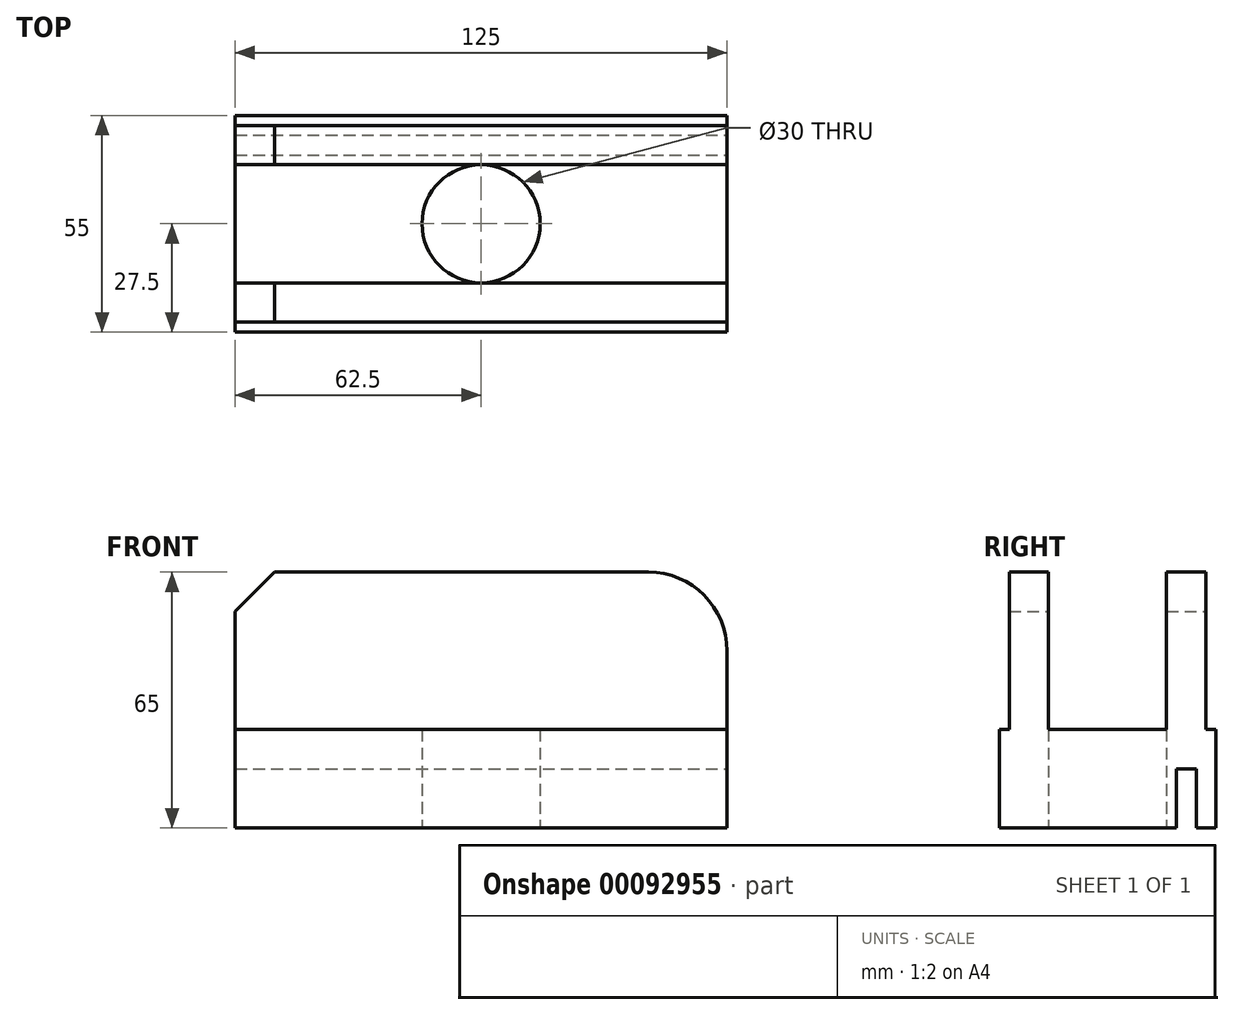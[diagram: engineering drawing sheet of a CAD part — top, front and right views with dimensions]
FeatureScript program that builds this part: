
annotation { "Feature Type Name" : "Feature", "Feature Type Description" : "" }
export const myFeature = defineFeature(function(context is Context, id is Id, definition is map)
    precondition{}
    {
        {
            var Q0;
            Q0=qCreatedBy(makeId("Top.planeOp"),FACE);
            var sketch = newSketch(context, id + "F0", { "sketchPlane" : qUnion([Q0])});
            skLineSegment(sketch, "E0.bottom", {"start": v(62.5, -27.5) * mm, "end": v(-62.5, -27.5) * mm});
            skLineSegment(sketch, "E0.top", {"start": v(62.5, 27.5) * mm, "end": v(-62.5, 27.5) * mm});
            skLineSegment(sketch, "E0.left", {"start": v(62.5, -27.5) * mm, "end": v(62.5, 27.5) * mm});
            skLineSegment(sketch, "E0.right", {"start": v(-62.5, -27.5) * mm, "end": v(-62.5, 27.5) * mm});
            skPoint(sketch, "E0.middle", {"position": v(0, 0) * mm});
            skCircle(sketch, "E1", {"center": v(0, 0) * mm, "radius": 15 * mm});
            skSolve(sketch);
        }
        {
            var Q0;
            Q0=qSketchRegion(id+"F0",true);
            extrude(context, id + "F1", {"entities" : qUnion([Q0]), "depth" : 25 * mm});
        }
        {
            var Q0;
            Q0=makeQuery(id+"F1.opExtrude","CAP_FACE",FACE,{"disambiguationData":[OSD([sQuery(id+"F0.wireOp",EDGE,"E0.bottom"),sQuery(id+"F0.wireOp",EDGE,"E0.top"),sQuery(id+"F0.wireOp",EDGE,"E0.left"),sQuery(id+"F0.wireOp",EDGE,"E0.right"),sQuery(id+"F0.wireOp",EDGE,"E1")])],"isStart":false});
            var sketch = newSketch(context, id + "F2", { "sketchPlane" : qUnion([Q0])});
            skLineSegment(sketch, "E2.bottom", {"start": v(-62.5, -25) * mm, "end": v(62.5, -25) * mm});
            skLineSegment(sketch, "E2.left", {"start": v(-62.5, -25) * mm, "end": v(-62.5, -15) * mm});
            skLineSegment(sketch, "E2.right", {"start": v(62.5, -25) * mm, "end": v(62.5, -15) * mm});
            skLineSegment(sketch, "E3.bottom", {"start": v(-62.5, -25) * mm, "end": v(-62.5, -25) * mm});
            skLineSegment(sketch, "E3.top", {"start": v(-62.5, -27.5) * mm, "end": v(-62.5, -27.5) * mm});
            skLineSegment(sketch, "E3.left", {"start": v(-62.5, -25) * mm, "end": v(-62.5, -27.5) * mm});
            skLineSegment(sketch, "E3.right", {"start": v(-62.5, -25) * mm, "end": v(-62.5, -27.5) * mm});
            skLineSegment(sketch, "E4", {"start": v(62.5, -15) * mm, "end": v(-62.5, -15) * mm});
            skLineSegment(sketch, "E5", {"start": v(0, 15) * mm, "end": v(62.5, 15) * mm});
            skLineSegment(sketch, "E6", {"start": v(62.5, 15) * mm, "end": v(62.5, 25) * mm});
            skLineSegment(sketch, "E7", {"start": v(62.5, 25) * mm, "end": v(-62.5, 25) * mm});
            skLineSegment(sketch, "E8", {"start": v(-62.5, 25) * mm, "end": v(-62.5, 15) * mm});
            skLineSegment(sketch, "E9", {"start": v(-62.5, 15) * mm, "end": v(0, 15) * mm});
            skSolve(sketch);
        }
        {
            var Q0;
            Q0=qSketchRegion(id+"F2",true);
            extrude(context, id + "F3", {"entities" : qUnion([Q0]), "operationType" : NewBodyOperationType.ADD, "depth" : 40 * mm});
        }
        {
            var Q0;
            Q0=makeQuery(id+"F3.opExtrude","CAP_EDGE",EDGE,{"disambiguationData":[OSD([sQuery(id+"F2.wireOp",EDGE,"E2.right")])],"isStart":false});
            var Q1;
            Q1=makeQuery(id+"F3.opExtrude","CAP_EDGE",EDGE,{"disambiguationData":[OSD([sQuery(id+"F2.wireOp",EDGE,"E6")])],"isStart":false});
            fillet(context, id + "F4", {"entities" : qUnion([Q0, Q1]), "radius" : 20 * mm, "tangentPropagation" : true, "allowEdgeOverflow" : false});
        }
        {
            var Q0;
            Q0=makeQuery(id+"F3.opExtrude","CAP_EDGE",EDGE,{"disambiguationData":[OSD([sQuery(id+"F2.wireOp",EDGE,"E8")])],"isStart":false});
            var Q1;
            Q1=makeQuery(id+"F3.opExtrude","CAP_EDGE",EDGE,{"disambiguationData":[OSD([sQuery(id+"F2.wireOp",EDGE,"E2.left")])],"isStart":false});
            chamfer(context, id + "F5", {"entities" : qUnion([Q0, Q1]), "width" : 10 * mm, "tangentPropagation" : true});
        }
        {
            var Q0;
            Q0=makeQuery(id+"F3.boolean.opBoolean","MERGE",FACE,{"derivedFrom":[makeQuery(id+"F1.opExtrude","SWEPT_FACE",FACE,{"disambiguationData":[OSD([sQuery(id+"F0.wireOp",EDGE,"E0.left")])]}),makeQuery(id+"F3.opExtrude","SWEPT_FACE",FACE,{"disambiguationData":[OSD([sQuery(id+"F2.wireOp",EDGE,"E2.right")])]}),makeQuery(id+"F3.opExtrude","SWEPT_FACE",FACE,{"disambiguationData":[OSD([sQuery(id+"F2.wireOp",EDGE,"E6")])]})]});
            var sketch = newSketch(context, id + "F6", { "sketchPlane" : qUnion([Q0])});
            skLineSegment(sketch, "E10.bottom", {"start": v(22.5, 15) * mm, "end": v(17.5, 15) * mm});
            skLineSegment(sketch, "E10.top", {"start": v(22.5, -15) * mm, "end": v(17.5, -15) * mm});
            skLineSegment(sketch, "E10.left", {"start": v(22.5, 15) * mm, "end": v(22.5, -15) * mm});
            skLineSegment(sketch, "E10.right", {"start": v(17.5, 15) * mm, "end": v(17.5, -15) * mm});
            skPoint(sketch, "E10.middle", {"position": v(20, 0) * mm});
            skPoint(sketch, "E11", {"position": v(20, 55) * mm});
            skSolve(sketch);
        }
        {
            var Q0;
            Q0=qSketchRegion(id+"F6",true);
            extrude(context, id + "F7", {"entities" : qUnion([Q0]), "operationType" : NewBodyOperationType.REMOVE, "endBound" : BoundingType.THROUGH_ALL, "oppositeDirection" : true, "depth" : 25 * mm});
        }
    });
